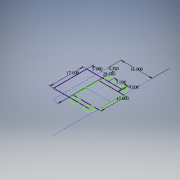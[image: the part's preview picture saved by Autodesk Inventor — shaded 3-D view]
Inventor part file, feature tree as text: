
AUTODESK INVENTOR PART (.ipt)
format: ipt  version: 2017 SP1 (Build 210196100, 196)  size: 97,280 bytes
history: native  units: in
note: dims shown in document units (in); Inventor stores cm internally (conversion verified against a paired STEP export)
features: sketch x1
ambient origin geometry x8: Origin, YZ Plane, XZ Plane, XY Plane, X Axis, Y Axis, Z Axis, Center Point
feature tree (1):
  sketch  "Sketch1"  dims[d0=28.0in d1=13.0in d2=3.25in d3=16.0in d4=4.0in d6=7.0in d7=5.0in d8=17.0in]
